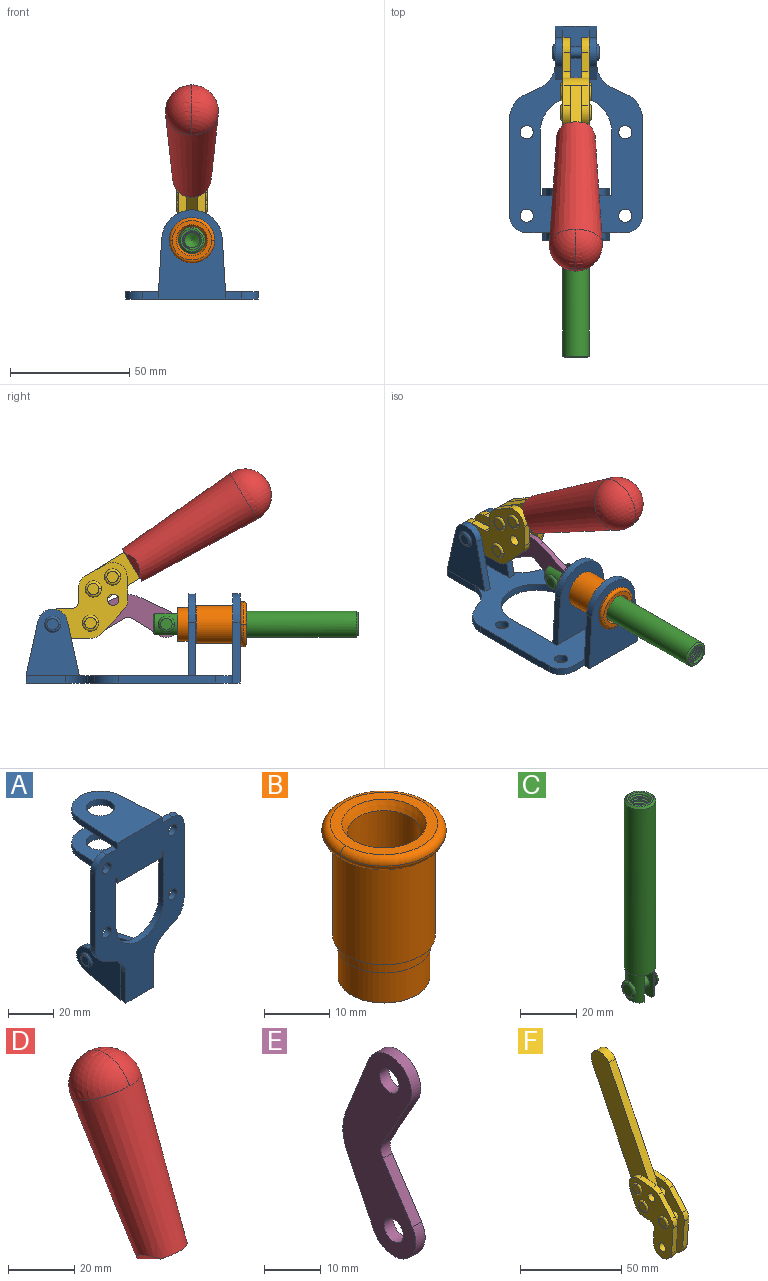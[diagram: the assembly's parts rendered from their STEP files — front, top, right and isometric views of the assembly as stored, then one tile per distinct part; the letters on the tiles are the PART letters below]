
ASSEMBLY  parts=6 mates=6
PART A: 55 faces, bbox 55.7x37.4x89.8 mm
  f0: torus R=2.41mm, axis (-1,0,0), area 15mm2, adj f11,f15,f25
  f1: torus R=2.41mm, axis (-1,0,0), area 15mm2, adj f10,f12,f22
  f2: cylinder r=2.78mm len=5.56mm, axis (0,-1,0), area 54.2mm2, adj f30,f54
  f3: cylinder r=14.99mm len=29.97mm, axis (0,-1,0), area 145.9mm2, adj f30,f49,f53,f54
  f4: cylinder r=2.78mm len=5.56mm, axis (0,-1,0), area 54.2mm2, adj f30,f54
  f5: cylinder r=2.78mm len=5.56mm, axis (0,-1,0), area 54.2mm2, adj f30,f54
  f6: cylinder r=2.78mm len=5.56mm, axis (0,-1,0), area 54.2mm2, adj f30,f54
  f7: cylinder r=6.35mm len=12.7mm, axis (0,0,1), area 123.6mm2, adj f27,f51
  f8: cylinder r=6.35mm len=12.7mm, axis (0,0,-1), area 124.7mm2, adj f21,f35
  f9: cylinder r=2.41mm len=11.18mm, axis (-1,0,0), area 169.4mm2, adj f16,f19
  f10: plane 4.83x4.83mm, normal (1,0,0), area 18.3mm2, adj f1,f12
  f11: plane 4.83x4.83mm, normal (-1,0,0), area 18.3mm2, adj f0,f15
  f12: torus R=2.41mm, axis (-1,0,0), area 15mm2, adj f1,f10,f22
  f13: cylinder r=6.35mm len=12.41mm, axis (1,0,0), area 53.4mm2, adj f18,f19,f22,f23
  f14: cylinder r=6.35mm len=12.41mm, axis (-1,0,0), area 53.4mm2, adj f16,f17,f24,f25
  f15: torus R=2.41mm, axis (-1,0,0), area 15mm2, adj f0,f11,f25
  f16: plane 27.86x22.35mm, normal (1,0,0), area 425.4mm2, adj f9,f14,f17,f24,f30
  f17: plane 22.86x4.97mm, normal (0,0.21,0.98), area 72.5mm2, adj f14,f16,f25,f30
  f18: plane 22.86x4.97mm, normal (0,0.21,0.98), area 72.5mm2, adj f13,f19,f22,f30
  f19: plane 27.86x22.35mm, normal (-1,0,0), area 425.4mm2, adj f9,f13,f18,f23,f30
  f20: cylinder r=12.7mm len=25.35mm, axis (0,0,-1), area 119.8mm2, adj f21,f34,f35,f36
  f21: plane 34.21x28.07mm, normal (0,0,-1), area 702.4mm2, adj f8,f20,f30,f34,f36
  f22: plane 27.96x22.45mm, normal (1,0,0), area 407.2mm2, adj f1,f12,f13,f18,f23,f30,f42,f43
  f23: plane 22.86x4.97mm, normal (0,0.21,-0.98), area 72.5mm2, adj f13,f19,f22,f44
  f24: plane 22.86x4.97mm, normal (0,0.21,-0.98), area 72.5mm2, adj f14,f16,f25,f44
  f25: plane 27.86x22.35mm, normal (-1,0,0), area 407.1mm2, adj f0,f14,f15,f17,f24,f30,f45,f46
  f26: plane 3.1x0.95mm, normal (0,0,-1), area 2.7mm2, adj f30,f49,f50,f54
  f27: plane 34.21x28.07mm, normal (0,0,1), area 702.4mm2, adj f7,f28,f30,f50,f52
  f28: cylinder r=12.7mm len=25.35mm, axis (0,0,1), area 118.8mm2, adj f27,f50,f51,f52
  f29: plane 3.1x0.95mm, normal (0,0,-1), area 2.7mm2, adj f30,f52,f53,f54
  f30: plane 86.54x55.63mm, normal (0,1,0), area 2362.9mm2, adj f2,f3,f4,f5,f6,f16,f17,f18
  f31: plane 40.56x3.1mm, normal (-1,0,0), area 125.7mm2, adj f30,f32,f48,f54
  f32: cylinder r=7.11mm len=7.11mm, axis (0,-1,0), area 34.6mm2, adj f30,f31,f33,f54
  f33: plane 6.67x3.1mm, normal (0,0,1), area 20.4mm2, adj f30,f32,f34,f54
  f34: plane 25.39x3.13mm, normal (-1,0.06,0), area 79.5mm2, adj f20,f21,f33,f35,f54
  f35: plane 37.31x28.45mm, normal (0,0,1), area 789.9mm2, adj f8,f20,f34,f36,f54
  f36: plane 25.39x3.13mm, normal (1,0.06,0), area 79.5mm2, adj f20,f21,f35,f37,f54
  f37: plane 6.67x3.1mm, normal (0,0,1), area 20.4mm2, adj f30,f36,f38,f54
  f38: cylinder r=7.11mm len=7.11mm, axis (0,-1,0), area 34.6mm2, adj f30,f37,f39,f54
  f39: plane 40.56x3.1mm, normal (1,0,0), area 125.7mm2, adj f30,f38,f40,f54
  f40: cylinder r=11.18mm len=10.16mm, axis (0,-1,0), area 39.5mm2, adj f30,f39,f41,f54
  f41: plane 6.09x3.1mm, normal (0.42,0,-0.91), area 20.8mm2, adj f30,f40,f42,f54
  f42: cylinder r=11.18mm len=9.41mm, axis (0,-1,0), area 37.2mm2, adj f22,f30,f41,f43,f54
  f43: plane 16.5x3.1mm, normal (1,0,0), area 51.1mm2, adj f22,f42,f44,f54
  f44: plane 17.37x3.1mm, normal (0,0,-1), area 53.8mm2, adj f23,f24,f30,f43,f45,f54
  f45: plane 16.5x3.1mm, normal (-1,0,0), area 51.1mm2, adj f25,f44,f46,f54
  f46: cylinder r=11.18mm len=9.41mm, axis (0,-1,0), area 37.2mm2, adj f25,f30,f45,f47,f54
  f47: plane 6.09x3.1mm, normal (-0.42,0,-0.91), area 20.8mm2, adj f30,f46,f48,f54
  f48: cylinder r=11.18mm len=10.16mm, axis (0,-1,0), area 39.5mm2, adj f30,f31,f47,f54
  f49: plane 26.54x3.1mm, normal (-1,0,0), area 82.3mm2, adj f3,f26,f30,f54
  f50: plane 25.39x3.1mm, normal (1,0.06,0), area 78.8mm2, adj f26,f27,f28,f51,f54
  f51: plane 37.31x28.45mm, normal (0,0,-1), area 789.9mm2, adj f7,f28,f50,f52,f54
  f52: plane 25.39x3.1mm, normal (-1,0.06,0), area 78.8mm2, adj f27,f28,f29,f51,f54
  f53: plane 26.54x3.1mm, normal (1,0,0), area 82.3mm2, adj f3,f29,f30,f54
  f54: plane 89.66x55.63mm, normal (0,-1,0), area 2678.5mm2, adj f2,f3,f4,f5,f6,f26,f29,f31
PART B: 15 faces, bbox 20.6x20.6x28.7 mm
  f0: torus R=8.26mm, axis (0,0,1), area 56.8mm2, adj f1,f10,f12
  f1: torus R=8.26mm, axis (0,0,1), area 56.8mm2, adj f0,f6,f13
  f2: cylinder r=5.59mm len=25.91mm, axis (0,0,1), area 909.6mm2, adj f3,f4
  f3: cone r=6.86mm half-angle=45deg, axis (0,0,-1), area 70.2mm2, adj f2,f14
  f4: cone r=6.47mm half-angle=30deg, axis (0,0,1), area 66.7mm2, adj f2,f13
  f5: cylinder r=7.04mm len=14.07mm, axis (0,0,1), area 252.6mm2, adj f11,f14
  f6: torus R=8.26mm, axis (0,0,1), area 56.8mm2, adj f1,f12,f13
  f7: cylinder r=7.16mm len=14.33mm, axis (0,0,1), area 91.5mm2, adj f9,f11
  f8: cylinder r=7.86mm len=18.42mm, axis (0,0,1), area 909.6mm2, adj f9,f10
  f9: plane 15.72x15.72mm, normal (0,0,-1), area 33mm2, adj f7,f8
  f10: plane 16.51x16.51mm, normal (0,0,-1), area 19.9mm2, adj f0,f8,f12
  f11: plane 14.33x14.33mm, normal (0,0,-1), area 5.7mm2, adj f5,f7
  f12: torus R=8.26mm, axis (0,0,1), area 56.8mm2, adj f0,f6,f10
  f13: plane 16.51x16.51mm, normal (0,0,1), area 82.7mm2, adj f1,f4,f6
  f14: plane 14.07x14.07mm, normal (0,0,-1), area 7.8mm2, adj f3,f5
PART C: 48 faces, bbox 12.6x11.1x86.1 mm
  f0: torus R=2.41mm, axis (-1,0,0), area 15mm2, adj f30,f32,f34
  f1: torus R=2.41mm, axis (-1,0,0), area 15mm2, adj f29,f31,f33
  f2: cylinder r=5.54mm len=72.39mm, axis (0,0,1), area 2518.5mm2, adj f3,f4,f42,f43
  f3: cone r=5.54mm half-angle=45deg, axis (0,0,1), area 7.6mm2, adj f2,f5,f41
  f4: cone r=5.54mm half-angle=45deg, axis (0,0,-1), area 34.9mm2, adj f2,f39
  f5: cylinder r=5.08mm len=11.48mm, axis (0,0,1), area 108.3mm2, adj f3,f7,f8,f41
  f6: cylinder r=2.41mm len=4.83mm, axis (-1,0,0), area 71.2mm2, adj f40,f41
  f7: cylinder r=2.41mm len=4.83mm, axis (-1,0,0), area 7.6mm2, adj f5,f34
  f8: cone r=5.08mm half-angle=45deg, axis (0,0,1), area 10.6mm2, adj f5,f37,f41
  f9: cone r=3.98mm half-angle=45deg, axis (0,0,1), area 17.6mm2, adj f27,f39,f45,f46,f47
  f10: cylinder r=2.41mm len=4.83mm, axis (-1,0,0), area 7.6mm2, adj f33,f38
  f11: cylinder r=3.2mm len=6.4mm, axis (0,0,1), area 78.4mm2, adj f12,f28,f44,f45,f47
  f12: cylinder r=3.2mm len=6.4mm, axis (0,0,1), area 10.5mm2, adj f11,f13,f45,f47
  f13: cylinder r=3.2mm len=6.4mm, axis (0,0,1), area 10.5mm2, adj f12,f14,f45,f47
  f14: cylinder r=3.2mm len=6.4mm, axis (0,0,1), area 10.5mm2, adj f13,f15,f45,f47
  f15: cylinder r=3.2mm len=6.4mm, axis (0,0,1), area 10.5mm2, adj f14,f16,f45,f47
  f16: cylinder r=3.2mm len=6.4mm, axis (0,0,1), area 10.5mm2, adj f15,f17,f45,f47
  f17: cylinder r=3.2mm len=6.4mm, axis (0,0,1), area 10.5mm2, adj f16,f18,f45,f47
  f18: cylinder r=3.2mm len=6.4mm, axis (0,0,1), area 10.5mm2, adj f17,f19,f45,f47
  f19: cylinder r=3.2mm len=6.4mm, axis (0,0,1), area 10.5mm2, adj f18,f20,f45,f47
  f20: cylinder r=3.2mm len=6.4mm, axis (0,0,1), area 10.5mm2, adj f19,f21,f45,f47
  f21: cylinder r=3.2mm len=6.4mm, axis (0,0,1), area 10.5mm2, adj f20,f22,f45,f47
  f22: cylinder r=3.2mm len=6.4mm, axis (0,0,1), area 10.5mm2, adj f21,f23,f45,f47
  f23: cylinder r=3.2mm len=6.4mm, axis (0,0,1), area 10.5mm2, adj f22,f24,f45,f47
  f24: cylinder r=3.2mm len=6.4mm, axis (0,0,1), area 10.5mm2, adj f23,f25,f45,f47
  f25: cylinder r=3.2mm len=6.4mm, axis (0,0,1), area 10.5mm2, adj f24,f26,f45,f47
  f26: cylinder r=3.2mm len=6.4mm, axis (0,0,1), area 10.5mm2, adj f25,f27,f45,f47
  f27: cylinder r=3.2mm len=6.4mm, axis (0,0,1), area 7.4mm2, adj f9,f26,f45,f47
  f28: cone r=3.2mm half-angle=60deg, axis (0,0,1), area 37.2mm2, adj f11
  f29: plane 4.83x4.83mm, normal (-1,0,0), area 18.3mm2, adj f1,f31
  f30: plane 4.83x4.83mm, normal (1,0,0), area 18.3mm2, adj f0,f32
  f31: torus R=2.41mm, axis (-1,0,0), area 15mm2, adj f1,f29,f33
  f32: torus R=2.41mm, axis (-1,0,0), area 15mm2, adj f0,f30,f34
  f33: plane 6.83x6.83mm, normal (1,0,0), area 18.3mm2, adj f1,f10,f31
  f34: plane 6.83x6.83mm, normal (-1,0,0), area 18.3mm2, adj f0,f7,f32
  f35: cone r=5.08mm half-angle=45deg, axis (0,0,1), area 10.6mm2, adj f36,f38,f40
  f36: plane 7.25x1.97mm, normal (0,0,-1), area 10mm2, adj f35,f40
  f37: plane 7.25x1.97mm, normal (0,0,-1), area 10mm2, adj f8,f41
  f38: cylinder r=5.08mm len=11.48mm, axis (0,0,1), area 108.3mm2, adj f10,f35,f40,f42
  f39: plane 9.55x9.55mm, normal (0,0,1), area 22mm2, adj f4,f9
  f40: plane 12.76x10.09mm, normal (1,0,0), area 95.7mm2, adj f6,f35,f36,f38,f42,f43
  f41: plane 12.76x10.09mm, normal (-1,0,0), area 95.7mm2, adj f3,f5,f6,f8,f37,f43
  f42: cone r=5.54mm half-angle=45deg, axis (0,0,1), area 7.6mm2, adj f2,f38,f40
  f43: plane 11.07x4.7mm, normal (0,0,-1), area 50.4mm2, adj f2,f40,f41
  f44: plane 0.89x0.62mm, normal (-1,0,0), area 0.3mm2, adj f11,f45,f46,f47
  f45: bspline ~24.8x7.63mm, area 266.6mm2, adj f9,f11,f12,f13,f14,f15,f16,f17
  f46: bspline ~24.87x7.63mm, area 73.6mm2, adj f9,f44,f45,f47
  f47: bspline ~24.98x7.63mm, area 272.5mm2, adj f9,f11,f12,f13,f14,f15,f16,f17
PART D: 11 faces, bbox 22.3x42.6x64.5 mm
  f0: sphere r=11.13mm, area 411.4mm2, adj f1,f8
  f1: cone r=11.11mm half-angle=3.3deg, axis (0,0.44,0.9), area 3251.8mm2, adj f0,f7,f8,f9,f10
  f2: cylinder r=6.16mm len=11.7mm, axis (1,0,0), area 89.5mm2, adj f3,f4,f5,f6
  f3: plane 60.23x36.75mm, normal (-1,0,0), area 763.6mm2, adj f2,f4,f6,f10
  f4: plane 51.37x25.05mm, normal (0,0.9,-0.44), area 264.2mm2, adj f2,f3,f5,f10
  f5: plane 60.23x36.75mm, normal (1,0,0), area 763.6mm2, adj f2,f4,f6,f10
  f6: plane 51.37x25.05mm, normal (0,-0.9,0.44), area 264.2mm2, adj f2,f3,f5,f10
  f7: plane 9.95x5.95mm, normal (0.71,-0.31,-0.64), area 25.8mm2, adj f1,f10
  f8: sphere r=11.13mm, area 411.4mm2, adj f0,f1
  f9: plane 9.95x5.95mm, normal (-0.71,-0.31,-0.64), area 25.8mm2, adj f1,f10
  f10: plane 14.27x11.38mm, normal (0,-0.44,-0.9), area 106.7mm2, adj f1,f3,f4,f5,f6,f7,f9
PART E: 12 faces, bbox 2.3x18.2x42.8 mm
  f0: cylinder r=2.4mm len=4.8mm, axis (1,0,0), area 34.9mm2, adj f4,f11
  f1: cylinder r=10.41mm len=8.47mm, axis (1,0,0), area 20.2mm2, adj f4,f9,f10,f11
  f2: cylinder r=3.05mm len=3.16mm, axis (1,0,0), area 7.7mm2, adj f4,f6,f7,f11
  f3: cylinder r=2.4mm len=4.8mm, axis (1,0,0), area 34.9mm2, adj f4,f11
  f4: plane 42.81x18.23mm, normal (-1,0,0), area 414.1mm2, adj f0,f1,f2,f3,f5,f6,f7,f8
  f5: cylinder r=5.54mm len=10.67mm, axis (1,0,0), area 41.8mm2, adj f4,f6,f10,f11
  f6: plane 11.66x6.53mm, normal (0,-0.87,-0.49), area 30.9mm2, adj f2,f4,f5,f11
  f7: plane 11.17x7.33mm, normal (0,-0.84,0.55), area 30.9mm2, adj f2,f4,f8,f11
  f8: cylinder r=5.54mm len=10.51mm, axis (1,0,0), area 41.8mm2, adj f4,f7,f9,f11
  f9: plane 13.67x6.67mm, normal (0,0.9,-0.44), area 35.1mm2, adj f1,f4,f8,f11
  f10: plane 14.1x5.7mm, normal (0,0.93,0.37), area 35.1mm2, adj f1,f4,f5,f11
  f11: plane 42.81x18.23mm, normal (1,0,0), area 414.1mm2, adj f0,f1,f2,f3,f5,f6,f7,f8
PART F: 59 faces, bbox 12.9x60.2x99.6 mm
  f0: torus R=2.39mm, axis (-1,0,0), area 14.9mm2, adj f20,f43,f51
  f1: torus R=2.39mm, axis (-1,0,0), area 14.9mm2, adj f19,f42,f51
  f2: torus R=2.39mm, axis (-1,0,0), area 14.9mm2, adj f18,f35,f51
  f3: torus R=2.39mm, axis (-1,0,0), area 14.9mm2, adj f14,f17,f23
  f4: torus R=2.39mm, axis (-1,0,0), area 14.9mm2, adj f13,f16,f23
  f5: torus R=2.39mm, axis (-1,0,0), area 14.9mm2, adj f12,f15,f23
  f6: cylinder r=2.39mm len=4.78mm, axis (1,0,0), area 46.5mm2, adj f48,f50,f51
  f7: cylinder r=2.39mm len=4.78mm, axis (1,0,0), area 46.5mm2, adj f50,f51
  f8: cylinder r=6.35mm len=12.68mm, axis (1,0,0), area 61.8mm2, adj f38,f39,f50,f51
  f9: cylinder r=2.39mm len=4.78mm, axis (-1,0,0), area 70.5mm2, adj f46,f50
  f10: cylinder r=2.39mm len=4.78mm, axis (-1,0,0), area 46.5mm2, adj f23,f45,f46
  f11: cylinder r=2.39mm len=4.78mm, axis (-1,0,0), area 46.5mm2, adj f23,f46
  f12: plane 4.78x4.78mm, normal (1,0,0), area 17.9mm2, adj f5,f15
  f13: plane 4.78x4.78mm, normal (1,0,0), area 17.9mm2, adj f4,f16
  f14: plane 4.78x4.78mm, normal (1,0,0), area 17.9mm2, adj f3,f17
  f15: torus R=2.39mm, axis (-1,0,0), area 14.9mm2, adj f5,f12,f23
  f16: torus R=2.39mm, axis (-1,0,0), area 14.9mm2, adj f4,f13,f23
  f17: torus R=2.39mm, axis (-1,0,0), area 14.9mm2, adj f3,f14,f23
  f18: plane 4.78x4.78mm, normal (-1,0,0), area 17.9mm2, adj f2,f35
  f19: plane 4.78x4.78mm, normal (-1,0,0), area 17.9mm2, adj f1,f42
  f20: plane 4.78x4.78mm, normal (-1,0,0), area 17.9mm2, adj f0,f43
  f21: plane 2.26x0.2mm, normal (1,0,0), area 0.2mm2, adj f31,f44
  f22: plane 2.26x0.2mm, normal (-1,0,0), area 0.2mm2, adj f41,f44
  f23: plane 39.37x30.77mm, normal (1,0,0), area 565.5mm2, adj f3,f4,f5,f10,f11,f15,f16,f17
  f24: cylinder r=6.1mm len=4.15mm, axis (-1,0,0), area 14.7mm2, adj f23,f25,f32,f46
  f25: plane 10.25x9.01mm, normal (0,-0.75,0.66), area 42.3mm2, adj f23,f24,f26,f46
  f26: cylinder r=6.35mm len=4.64mm, axis (-1,0,0), area 15.6mm2, adj f23,f25,f27,f46
  f27: plane 15.84x3.1mm, normal (0,-1,-0.07), area 49.2mm2, adj f23,f26,f28,f46
  f28: cylinder r=6.35mm len=12.68mm, axis (-1,0,0), area 61.8mm2, adj f23,f27,f29,f46
  f29: plane 8.11x3.1mm, normal (0,1,0.07), area 25.2mm2, adj f23,f28,f30,f46
  f30: cylinder r=3.05mm len=3.25mm, axis (-1,0,0), area 14.8mm2, adj f23,f29,f31,f46
  f31: plane 5.99x3.1mm, normal (0,0.07,-1), area 18.6mm2, adj f21,f23,f30,f44,f46
  f32: plane 9.5x3.1mm, normal (0,-0.07,1), area 29.5mm2, adj f23,f24,f33,f46,f47
  f33: cylinder r=6.1mm len=8.63mm, axis (-1,0,0), area 39.1mm2, adj f23,f32,f34,f47
  f34: plane 8.65x3.96mm, normal (0,0.91,-0.42), area 29.5mm2, adj f23,f33,f44,f47
  f35: torus R=2.39mm, axis (-1,0,0), area 14.9mm2, adj f2,f18,f51
  f36: plane 10.25x9.01mm, normal (0,-0.75,0.66), area 42.3mm2, adj f37,f49,f50,f51
  f37: cylinder r=6.35mm len=4.64mm, axis (1,0,0), area 15.6mm2, adj f36,f38,f50,f51
  f38: plane 15.84x3.1mm, normal (0,-1,-0.07), area 49.2mm2, adj f8,f37,f50,f51
  f39: plane 8.11x3.1mm, normal (0,1,0.07), area 25.2mm2, adj f8,f40,f50,f51
  f40: cylinder r=3.05mm len=3.25mm, axis (1,0,0), area 14.8mm2, adj f39,f41,f50,f51
  f41: plane 5.99x3.1mm, normal (0,0.07,-1), area 18.6mm2, adj f22,f40,f44,f50,f51
  f42: torus R=2.39mm, axis (-1,0,0), area 14.9mm2, adj f1,f19,f51
  f43: torus R=2.39mm, axis (-1,0,0), area 14.9mm2, adj f0,f20,f51
  f44: cylinder r=6.35mm len=12.12mm, axis (-1,0,0), area 128.9mm2, adj f21,f22,f23,f31,f34,f41,f46,f47
  f45: plane 2.65x1.35mm, normal (1,0,0), area 1mm2, adj f10,f55
  f46: plane 39.08x20.42mm, normal (-1,0,0), area 412.5mm2, adj f9,f10,f11,f24,f25,f26,f27,f28
  f47: plane 77.62x39.82mm, normal (1,0,0), area 850mm2, adj f32,f33,f34,f44,f53,f54,f55
  f48: plane 2.65x1.35mm, normal (-1,0,0), area 1mm2, adj f6,f55
  f49: cylinder r=6.1mm len=4.15mm, axis (1,0,0), area 14.7mm2, adj f36,f50,f51,f56
  f50: plane 39.08x20.42mm, normal (1,0,0), area 412.5mm2, adj f6,f7,f8,f9,f36,f37,f38,f39
  f51: plane 39.37x30.77mm, normal (-1,0,0), area 565.5mm2, adj f0,f1,f2,f6,f7,f8,f35,f36
  f52: plane 8.65x3.96mm, normal (0,0.91,-0.42), area 29.5mm2, adj f44,f51,f57,f58
  f53: plane 68.49x33.4mm, normal (0,0.9,-0.44), area 358.1mm2, adj f44,f47,f54,f58
  f54: cylinder r=6.35mm len=12.06mm, axis (1,0,0), area 93.7mm2, adj f47,f53,f55,f58
  f55: plane 68.49x33.4mm, normal (0,-0.9,0.44), area 358.1mm2, adj f44,f45,f46,f47,f48,f50,f54,f58
  f56: plane 9.5x3.1mm, normal (0,-0.07,1), area 29.5mm2, adj f49,f50,f51,f57,f58
  f57: cylinder r=6.1mm len=8.63mm, axis (1,0,0), area 39.1mm2, adj f51,f52,f56,f58
  f58: plane 77.62x39.82mm, normal (-1,0,0), area 850mm2, adj f44,f52,f53,f54,f55,f56,f57
PLACE A rot(axis=(1,0,0),90deg) t=(0,9.14,0)mm fixed
PLACE B rot(axis=(1,0,0),90deg) t=(0,9.14,0)mm
PLACE C rot(axis=(1,0,0),90deg) t=(0,9.09,0)mm
PLACE D rot(axis=(1,0,0),84.3deg) t=(-0.04,6.87,3.28)mm
PLACE E rot(axis=(1,0,0),92.8deg) t=(0,10.29,0.79)mm
PLACE F rot(axis=(1,0,0),84.3deg) t=(0,6.87,3.28)mm
MATE revolute F.f7 <-> A.f0  axis (-1,0,0) through (0,41.23,24.61)mm
MATE revolute F.f4 <-> E.f3  axis (-1,0,0) through (0,25.36,25.07)mm
MATE revolute C.f6 <-> E.f5  axis (-1,0,0) through (0,-6.38,24.61)mm
MATE fastened B.f2 <-> A.f7  axis (0,1,0) through (0,-37.25,24.61)mm
MATE fastened D.f2 <-> F.f54  axis (1,0,0) through (-2.35,-40.64,79.37)mm
MATE slider B.f2 <-> C.f2  axis (0,-1,0) through (0,-38.27,24.61)mm
